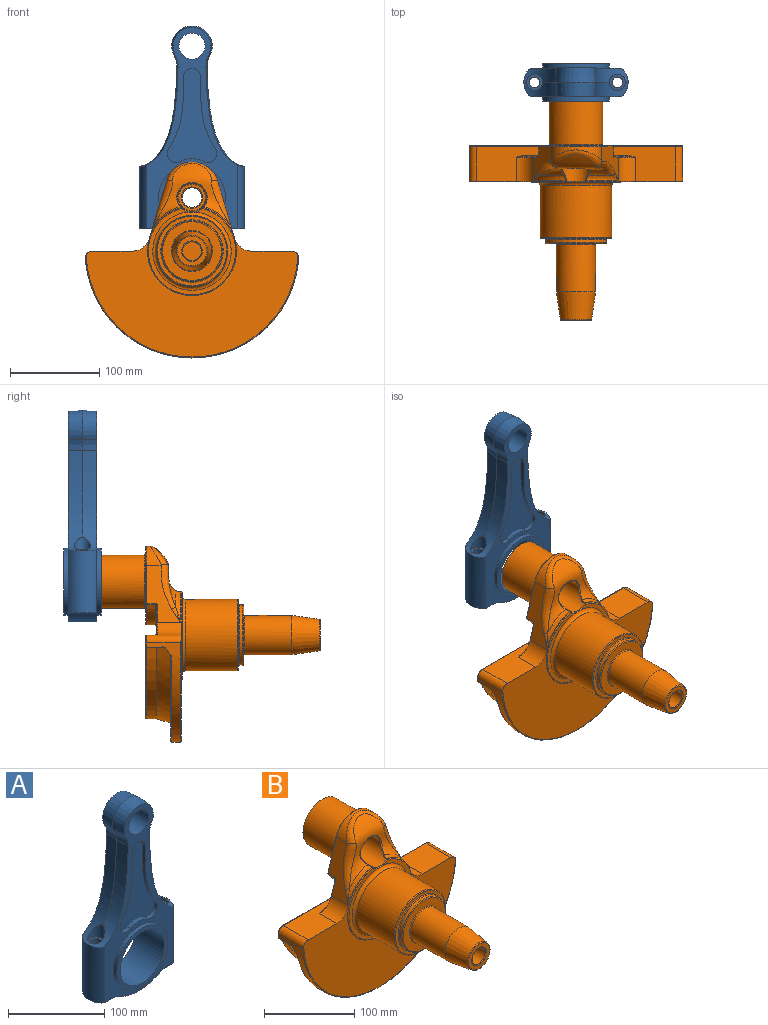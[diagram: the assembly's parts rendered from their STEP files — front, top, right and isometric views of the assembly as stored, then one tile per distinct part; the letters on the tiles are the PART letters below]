
ASSEMBLY  parts=2 mates=1
PART A: 49 faces, bbox 120.2x42.2x237.8 mm
  f0: cylinder r=6mm len=67.5mm, axis (0,0,-1), area 2544.7mm2, adj f11,f36
  f1: cylinder r=6mm len=67.5mm, axis (0,0,-1), area 2544.7mm2, adj f9,f33
  f2: bspline ~121.67x44.68mm, area 1865.6mm2, adj f4,f5,f32,f35,f40
  f3: bspline ~121.67x44.68mm, area 1865.6mm2, adj f4,f6,f31,f34,f37
  f4: plane 236.43x102.38mm, normal (0,-1,0), area 6386mm2, adj f2,f3,f8,f9,f10,f11,f12,f14
  f5: bspline ~121.67x44.68mm, area 1865.6mm2, adj f2,f7,f32,f35,f41
  f6: bspline ~121.67x44.68mm, area 1865.6mm2, adj f3,f7,f31,f34,f38
  f7: plane 236.43x102.38mm, normal (0,1,0), area 6386mm2, adj f5,f6,f9,f10,f11,f21,f22,f23
  f8: cone r=22.67mm half-angle=5deg, axis (0,1,0), area 1458.2mm2, adj f4,f22,f37,f40
  f9: plane 32x21.08mm, normal (0,0,-1), area 489.2mm2, adj f1,f4,f7,f31,f47
  f10: cylinder r=65mm len=64.86mm, axis (0,1,0), area 2172.8mm2, adj f4,f7,f47,f48
  f11: plane 32x21.08mm, normal (0,0,-1), area 489.2mm2, adj f0,f4,f7,f32,f48
  f12: cylinder r=37.5mm len=75mm, axis (0,1,0), area 1178.1mm2, adj f4,f13
  f13: plane 75x75mm, normal (0,-1,0), area 1099.6mm2, adj f12,f20
  f14: plane 26.04x5mm, normal (-1,0,0), area 130.2mm2, adj f4,f15,f19,f45
  f15: cylinder r=10mm len=20mm, axis (0,-1,0), area 157.1mm2, adj f4,f14,f16,f19
  f16: plane 26.04x5mm, normal (1,0,0), area 130.2mm2, adj f4,f15,f19,f46
  f17: cylinder r=10mm len=15.43mm, axis (0,-1,0), area 133.6mm2, adj f4,f19,f42,f46
  f18: cylinder r=10mm len=15.43mm, axis (0,-1,0), area 133.6mm2, adj f4,f19,f42,f45
  f19: plane 105.76x55.24mm, normal (0,-1,0), area 3030.8mm2, adj f14,f15,f16,f17,f18,f42,f45,f46
  f20: cylinder r=32.5mm len=65mm, axis (0,1,0), area 8576.5mm2, adj f13,f24
  f21: cylinder r=14.67mm len=32mm, axis (0,1,0), area 2949.9mm2, adj f4,f7
  f22: cone r=22.67mm half-angle=5deg, axis (0,-1,0), area 1458.2mm2, adj f7,f8,f38,f41
  f23: cylinder r=37.5mm len=75mm, axis (0,-1,0), area 1178.1mm2, adj f7,f24
  f24: plane 75x75mm, normal (0,1,0), area 1099.6mm2, adj f20,f23
  f25: plane 26.04x5mm, normal (-1,0,0), area 130.2mm2, adj f7,f26,f30,f44
  f26: cylinder r=10mm len=20mm, axis (0,1,0), area 157.1mm2, adj f7,f25,f27,f30
  f27: plane 26.04x5mm, normal (1,0,0), area 130.2mm2, adj f7,f26,f30,f43
  f28: cylinder r=10mm len=15.43mm, axis (0,1,0), area 133.6mm2, adj f7,f30,f39,f43
  f29: cylinder r=10mm len=15.43mm, axis (0,1,0), area 133.6mm2, adj f7,f30,f39,f44
  f30: plane 105.76x55.24mm, normal (0,1,0), area 3030.8mm2, adj f25,f26,f27,f28,f29,f39,f43,f44
  f31: cylinder r=21mm len=71.39mm, axis (0,0,-1), area 2576.3mm2, adj f3,f4,f6,f7,f9
  f32: cylinder r=21mm len=71.39mm, axis (0,0,-1), area 2576.3mm2, adj f2,f4,f5,f7,f11
  f33: plane 18x18mm, normal (0,0,1), area 141.4mm2, adj f1,f34
  f34: cylinder r=9mm len=18mm, axis (0,0,-1), area 586.6mm2, adj f3,f6,f33
  f35: cylinder r=9mm len=18mm, axis (0,0,-1), area 493.9mm2, adj f2,f5,f36
  f36: plane 18x18mm, normal (0,0,1), area 141.4mm2, adj f0,f35
  f37: bspline ~21.04x12.69mm, area 202.6mm2, adj f3,f4,f8,f38
  f38: bspline ~21.04x12.69mm, area 202.6mm2, adj f6,f7,f22,f37
  f39: cylinder r=25mm len=25.17mm, axis (0,1,0), area 131.9mm2, adj f7,f28,f29,f30
  f40: bspline ~21.04x12.69mm, area 202.6mm2, adj f2,f4,f8,f41
  f41: bspline ~21.04x12.69mm, area 202.6mm2, adj f5,f7,f22,f40
  f42: cylinder r=25mm len=25.17mm, axis (0,-1,0), area 131.9mm2, adj f4,f17,f18,f19
  f43: cylinder r=100mm len=54.29mm, axis (0,1,0), area 286.9mm2, adj f7,f27,f28,f30
  f44: cylinder r=100mm len=54.29mm, axis (0,1,0), area 286.9mm2, adj f7,f25,f29,f30
  f45: cylinder r=100mm len=54.29mm, axis (0,-1,0), area 286.9mm2, adj f4,f14,f18,f19
  f46: cylinder r=100mm len=54.29mm, axis (0,-1,0), area 286.9mm2, adj f4,f16,f17,f19
  f47: cylinder r=10mm len=32mm, axis (0,1,0), area 167.1mm2, adj f4,f7,f9,f10
  f48: cylinder r=10mm len=32mm, axis (0,1,0), area 167.1mm2, adj f4,f7,f10,f11
PART B: 101 faces, bbox 259.6x246x232.4 mm
  f0: cylinder r=50mm len=36.05mm, axis (0,1,0), area 42.4mm2, adj f35,f37,f48,f53
  f1: plane 237.43x92mm, normal (0,1,0), area 16224.2mm2, adj f89,f90,f91,f92,f93,f94,f95,f96
  f2: plane 98x96.6mm, normal (0,-1,0), area 1372.1mm2, adj f46,f52,f53,f57
  f3: cylinder r=50mm len=36.05mm, axis (0,1,0), area 42.4mm2, adj f36,f38,f53,f54
  f4: plane 86.65x81.31mm, normal (0,1,0), area 2091.3mm2, adj f70,f74,f78,f79,f100
  f5: plane 64.29x38.19mm, normal (-0.96,0,0.29), area 1272.1mm2, adj f6,f36,f42,f43,f68,f70,f71,f72
  f6: cylinder r=30mm len=57.5mm, axis (0,-1,0), area 676.5mm2, adj f5,f7,f41,f74
  f7: plane 64.29x38.19mm, normal (0.96,0,0.29), area 1272.1mm2, adj f6,f35,f39,f40,f77,f78,f80,f82
  f8: plane 223.43x39mm, normal (0,0,1), area 4836.7mm2, adj f9,f35,f36,f44,f45,f65,f67,f69
  f9: plane 237.83x133.29mm, normal (0,-1,0), area 18403mm2, adj f8,f35,f36,f44,f45,f53,f64
  f10: cylinder r=120mm len=239.39mm, axis (0,-1,0), area 3826.2mm2, adj f30,f31,f44,f45,f64,f83,f84,f86
  f11: cylinder r=40mm len=80mm, axis (0,-1,0), area 14577mm2, adj f46,f58
  f12: plane 78x78mm, normal (0,-1,0), area 929.9mm2, adj f58,f59
  f13: cylinder r=34mm len=68mm, axis (0,-1,0), area 854.5mm2, adj f59,f60
  f14: plane 66x66mm, normal (0,-1,0), area 1759.3mm2, adj f60,f61
  f15: cylinder r=22mm len=53mm, axis (0,-1,0), area 7326.2mm2, adj f16,f61
  f16: cone r=22mm half-angle=8deg, axis (0,1,0), area 3914.3mm2, adj f15,f63
  f17: plane 33.27x33.27mm, normal (0,-1,0), area 453.5mm2, adj f62,f63
  f18: cylinder r=30mm len=60mm, axis (0,-1,0), area 9236.3mm2, adj f19,f100
  f19: plane 60x60mm, normal (0,1,0), area 1306.9mm2, adj f18,f99
  f20: cylinder r=21mm len=42mm, axis (0,1,0), area 3166.7mm2, adj f21,f99
  f21: plane 42x42mm, normal (0,1,0), area 1005.3mm2, adj f20,f23
  f22: revolved ~157.26x67.43mm, area 1906.6mm2, adj f37,f38,f40,f41,f42,f49
  f23: cylinder r=11mm len=24mm, axis (0,1,0), area 1658.8mm2, adj f21,f97
  f24: cylinder r=16mm len=39mm, axis (0,1,0), area 2875.5mm2, adj f47,f48,f49,f51,f52,f54,f55,f57
  f25: plane 30x30mm, normal (0,-1,0), area 254.5mm2, adj f97,f98
  f26: cylinder r=10.5mm len=29mm, axis (0,-1,0), area 1913.7mm2, adj f27,f62
  f27: plane 21.01x21.01mm, normal (0,-1,0), area 346.5mm2, adj f26
  f28: cone r=124mm half-angle=17deg, axis (0,-1,0), area 4998.2mm2, adj f30,f31,f32,f83,f85,f88
  f29: plane 230.56x89.48mm, normal (0,1,0), area 3734.6mm2, adj f85,f86
  f30: plane 20.74x2.73mm, normal (-0.34,0,-0.94), area 45.7mm2, adj f10,f28,f32,f88,f93
  f31: plane 20.74x2.73mm, normal (0.34,0,-0.94), area 45.7mm2, adj f10,f28,f32,f83,f89
  f32: cylinder r=124mm len=233.04mm, axis (0,1,0), area 3332.9mm2, adj f28,f30,f31,f91
  f33: plane 116.28x31.6mm, normal (0,1,0), area 1670.7mm2, adj f66,f67,f68,f73,f76,f77
  f34: cylinder r=48.65mm len=83.02mm, axis (0,1,0), area 994.4mm2, adj f71,f76,f79,f82
  f35: cylinder r=20mm len=27mm, axis (0,1,0), area 691.8mm2, adj f0,f7,f8,f9,f73
  f36: cylinder r=20mm len=27mm, axis (0,1,0), area 691.8mm2, adj f3,f5,f8,f9,f66
  f37: torus R=60mm, axis (0,1,0), area 244.1mm2, adj f0,f22,f39,f47
  f38: torus R=60mm, axis (0,1,0), area 244.1mm2, adj f3,f22,f43,f51
  f39: bspline ~16.75x9.66mm, area 48.2mm2, adj f7,f37,f40
  f40: bspline ~54.37x22.51mm, area 536mm2, adj f7,f22,f39,f41
  f41: bspline ~57.97x22.63mm, area 568.9mm2, adj f6,f22,f40,f42
  f42: bspline ~52.49x21.91mm, area 536mm2, adj f5,f22,f41,f43
  f43: bspline ~16.75x9.66mm, area 48.2mm2, adj f5,f38,f42
  f44: cylinder r=8mm len=39mm, axis (0,-1,0), area 510.3mm2, adj f8,f9,f10,f64,f96
  f45: cylinder r=8mm len=39mm, axis (0,-1,0), area 510.3mm2, adj f8,f9,f10,f64,f92
  f46: torus R=44mm, axis (0,-1,0), area 1631.2mm2, adj f2,f11,f55
  f47: bspline ~9.18x2.74mm, area 6.4mm2, adj f24,f37,f48,f49
  f48: cylinder r=1mm len=0.92mm, axis (0,1,0), area 0.8mm2, adj f0,f24,f47,f50
  f49: bspline ~34.13x27.92mm, area 122.6mm2, adj f22,f24,f47,f51
  f50: sphere r=1mm, area 1mm2, adj f48,f52,f53
  f51: bspline ~9.18x2.74mm, area 6.4mm2, adj f24,f38,f49,f54
  f52: torus R=17mm, axis (0,-1,0), area 11.8mm2, adj f2,f24,f50,f55
  f53: torus R=49mm, axis (0,-1,0), area 452.5mm2, adj f0,f2,f3,f9,f50,f56
  f54: cylinder r=1mm len=0.92mm, axis (0,-1,0), area 0.8mm2, adj f3,f24,f51,f56
  f55: bspline ~12.15x1.91mm, area 13.8mm2, adj f24,f46,f52,f57
  f56: sphere r=1mm, area 1mm2, adj f53,f54,f57
  f57: torus R=17mm, axis (0,-1,0), area 11.8mm2, adj f2,f24,f55,f56
  f58: torus R=39mm, axis (0,1,0), area 391.2mm2, adj f11,f12
  f59: torus R=35mm, axis (0,1,0), area 339.2mm2, adj f12,f13
  f60: torus R=33mm, axis (0,1,0), area 332mm2, adj f13,f14
  f61: torus R=23mm, axis (0,1,0), area 220.7mm2, adj f14,f15
  f62: torus R=11.5mm, axis (0,-1,0), area 107.2mm2, adj f17,f26
  f63: torus R=16.63mm, axis (0,-1,0), area 155mm2, adj f16,f17
  f64: torus R=119mm, axis (0,-1,0), area 569.8mm2, adj f9,f10,f44,f45
  f65: bspline ~9.57x2mm, area 4.6mm2, adj f8,f66,f67
  f66: torus R=21mm, axis (0,-1,0), area 33.9mm2, adj f33,f36,f65,f68
  f67: cylinder r=1mm len=116.28mm, axis (-1,0,0), area 182.6mm2, adj f8,f33,f65,f69
  f68: cylinder r=1mm len=18.89mm, axis (-0.29,0,-0.96), area 30.5mm2, adj f5,f33,f66,f72
  f69: bspline ~9.57x2mm, area 4.6mm2, adj f8,f67,f73
  f70: cylinder r=1mm len=43.43mm, axis (-0.29,0,-0.96), area 70.7mm2, adj f4,f5,f74,f75
  f71: cylinder r=1mm len=10mm, axis (0,1,0), area 8.4mm2, adj f5,f34,f72,f75
  f72: bspline ~2.96x2.36mm, area 3.3mm2, adj f5,f68,f71,f76
  f73: torus R=21mm, axis (0,-1,0), area 33.9mm2, adj f33,f35,f69,f77
  f74: torus R=29mm, axis (0,-1,0), area 119.3mm2, adj f4,f6,f70,f78
  f75: sphere r=1mm, area 0.6mm2, adj f70,f71,f79
  f76: torus R=49.65mm, axis (0,-1,0), area 154.6mm2, adj f33,f34,f72,f80
  f77: cylinder r=1mm len=18.89mm, axis (-0.29,0,0.96), area 30.5mm2, adj f7,f33,f73,f80
  f78: cylinder r=1mm len=43.43mm, axis (-0.29,0,0.96), area 70.7mm2, adj f4,f7,f74,f81
  f79: torus R=47.65mm, axis (0,-1,0), area 155mm2, adj f4,f34,f75,f81
  f80: bspline ~3.33x2.22mm, area 3.3mm2, adj f7,f76,f77,f82
  f81: sphere r=1mm, area 0.6mm2, adj f78,f79,f82
  f82: cylinder r=1mm len=10mm, axis (0,1,0), area 8.4mm2, adj f7,f34,f80,f81
  f83: bspline ~21.98x16.93mm, area 3.9mm2, adj f10,f28,f31,f84
  f84: bspline ~9.6x3.23mm, area 8.9mm2, adj f10,f83,f85,f86
  f85: torus R=129.74mm, axis (0,1,0), area 370.6mm2, adj f28,f29,f84,f87
  f86: torus R=119mm, axis (0,1,0), area 496.1mm2, adj f10,f29,f84,f87
  f87: bspline ~11.03x3.76mm, area 8.9mm2, adj f10,f85,f86,f88
  f88: bspline ~21.98x16.93mm, area 3.9mm2, adj f10,f28,f30,f87
  f89: cylinder r=1mm len=4.01mm, axis (-0.94,0,-0.34), area 4.3mm2, adj f1,f31,f90,f91
  f90: torus R=119mm, axis (0,-1,0), area 6.6mm2, adj f1,f10,f89,f92
  f91: torus R=123mm, axis (0,-1,0), area 476.1mm2, adj f1,f32,f89,f93
  f92: torus R=7mm, axis (0,-1,0), area 19.7mm2, adj f1,f45,f90,f94
  f93: cylinder r=1mm len=4.01mm, axis (-0.94,0,0.34), area 4.3mm2, adj f1,f30,f91,f95
  f94: cylinder r=1mm len=223.43mm, axis (-1,0,0), area 351mm2, adj f1,f8,f92,f96
  f95: torus R=119mm, axis (0,-1,0), area 6.6mm2, adj f1,f10,f93,f96
  f96: torus R=7mm, axis (0,-1,0), area 19.7mm2, adj f1,f44,f94,f95
  f97: torus R=12mm, axis (0,1,0), area 112.2mm2, adj f23,f25
  f98: torus R=15mm, axis (0,1,0), area 154.3mm2, adj f24,f25
  f99: torus R=22mm, axis (0,1,0), area 210.8mm2, adj f19,f20
  f100: torus R=31mm, axis (0,-1,0), area 299.7mm2, adj f4,f18
PLACE A t=(-1.95,111.41,56.37)mm
PLACE B t=(-1.95,0.41,-3.63)mm fixed
MATE cylindrical A.f20 <-> B.f18  axis (0,1,0) through (-1.95,90.41,56.37)mm
